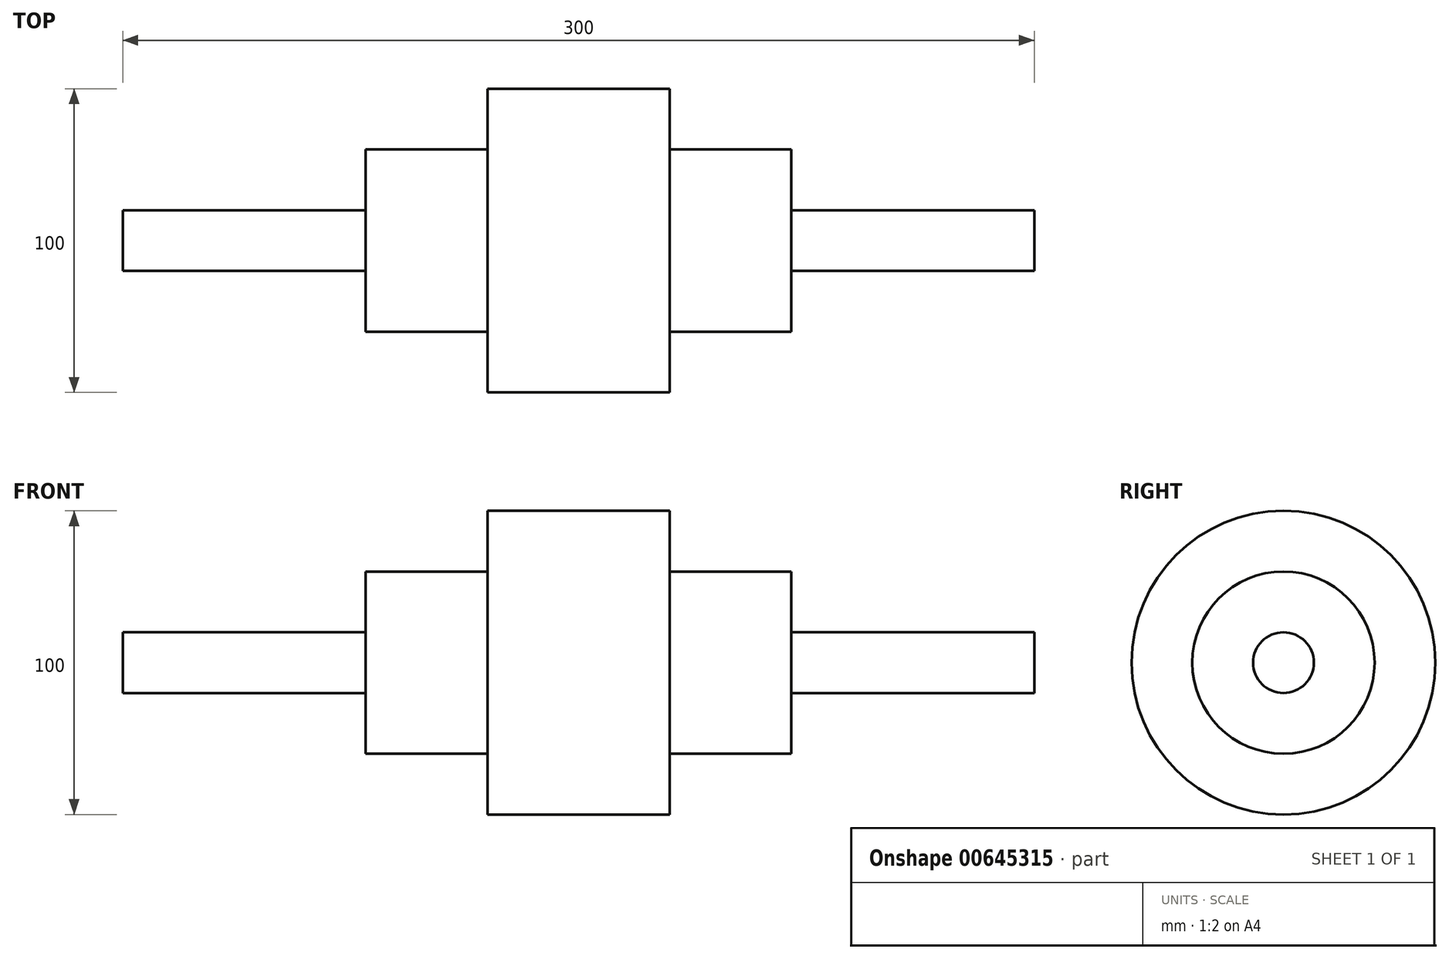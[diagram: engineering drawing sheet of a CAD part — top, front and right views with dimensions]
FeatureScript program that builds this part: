
annotation { "Feature Type Name" : "Feature", "Feature Type Description" : "" }
export const myFeature = defineFeature(function(context is Context, id is Id, definition is map)
    precondition{}
    {
        {
            var Q0;
            Q0=qCreatedBy(makeId("Front.planeOp"),FACE);
            var sketch = newSketch(context, id + "F0", { "sketchPlane" : qUnion([Q0])});
            skLineSegment(sketch, "E0.bottom", {"start": v(0, 0) * mm, "end": v(-60, 0) * mm});
            skLineSegment(sketch, "E0.top", {"start": v(0, 50) * mm, "end": v(-60, 50) * mm});
            skLineSegment(sketch, "E0.left", {"start": v(0, 0) * mm, "end": v(0, 50) * mm});
            skLineSegment(sketch, "E0.right", {"start": v(-60, 0) * mm, "end": v(-60, 50) * mm});
            skLineSegment(sketch, "E1", {"start": v(-60, 30) * mm, "end": v(-100, 30) * mm});
            skLineSegment(sketch, "E2", {"start": v(-100, 30) * mm, "end": v(-100, 0) * mm});
            skLineSegment(sketch, "E3", {"start": v(-100, 0) * mm, "end": v(-60, 0) * mm});
            skLineSegment(sketch, "E4", {"start": v(0, 30) * mm, "end": v(40, 30) * mm});
            skLineSegment(sketch, "E5", {"start": v(40, 30) * mm, "end": v(40, 0) * mm});
            skLineSegment(sketch, "E6", {"start": v(40, 0) * mm, "end": v(0, 0) * mm});
            skLineSegment(sketch, "E7", {"start": v(40, 10) * mm, "end": v(120, 10) * mm});
            skLineSegment(sketch, "E8", {"start": v(120, 10) * mm, "end": v(120, 0) * mm});
            skLineSegment(sketch, "E9", {"start": v(120, 0) * mm, "end": v(40, 0) * mm});
            skLineSegment(sketch, "E10", {"start": v(-100, 10) * mm, "end": v(-180, 10) * mm});
            skLineSegment(sketch, "E11", {"start": v(-180, 10) * mm, "end": v(-180, 0) * mm});
            skLineSegment(sketch, "E12", {"start": v(-180, 0) * mm, "end": v(-100, 0) * mm});
            skSolve(sketch);
        }
        {
            var Q0;
            Q0=qCreatedBy(makeId("Front.planeOp"),FACE);
            var sketch = newSketch(context, id + "F1", { "sketchPlane" : qUnion([Q0])});
            skLineSegment(sketch, "E13", {"start": v(0, 0) * mm, "end": v(-175, 0) * mm, "construction": true});
            skLineSegment(sketch, "E14", {"start": v(-175, 0) * mm, "end": v(175, 0) * mm, "construction": true});
            skSolve(sketch);
        }
        {
            var Q0;
            Q0 = qSketchRegion(id + "F0", true);
            var Q1;
            Q1=sQuery(id+"F1.wireOp",EDGE,"E14");
            revolve(context, id + "F2", {"entities" : qUnion([Q0]), "axis" : qUnion([Q1]), "revolveType" : RevolveType.FULL});
        }
    });
